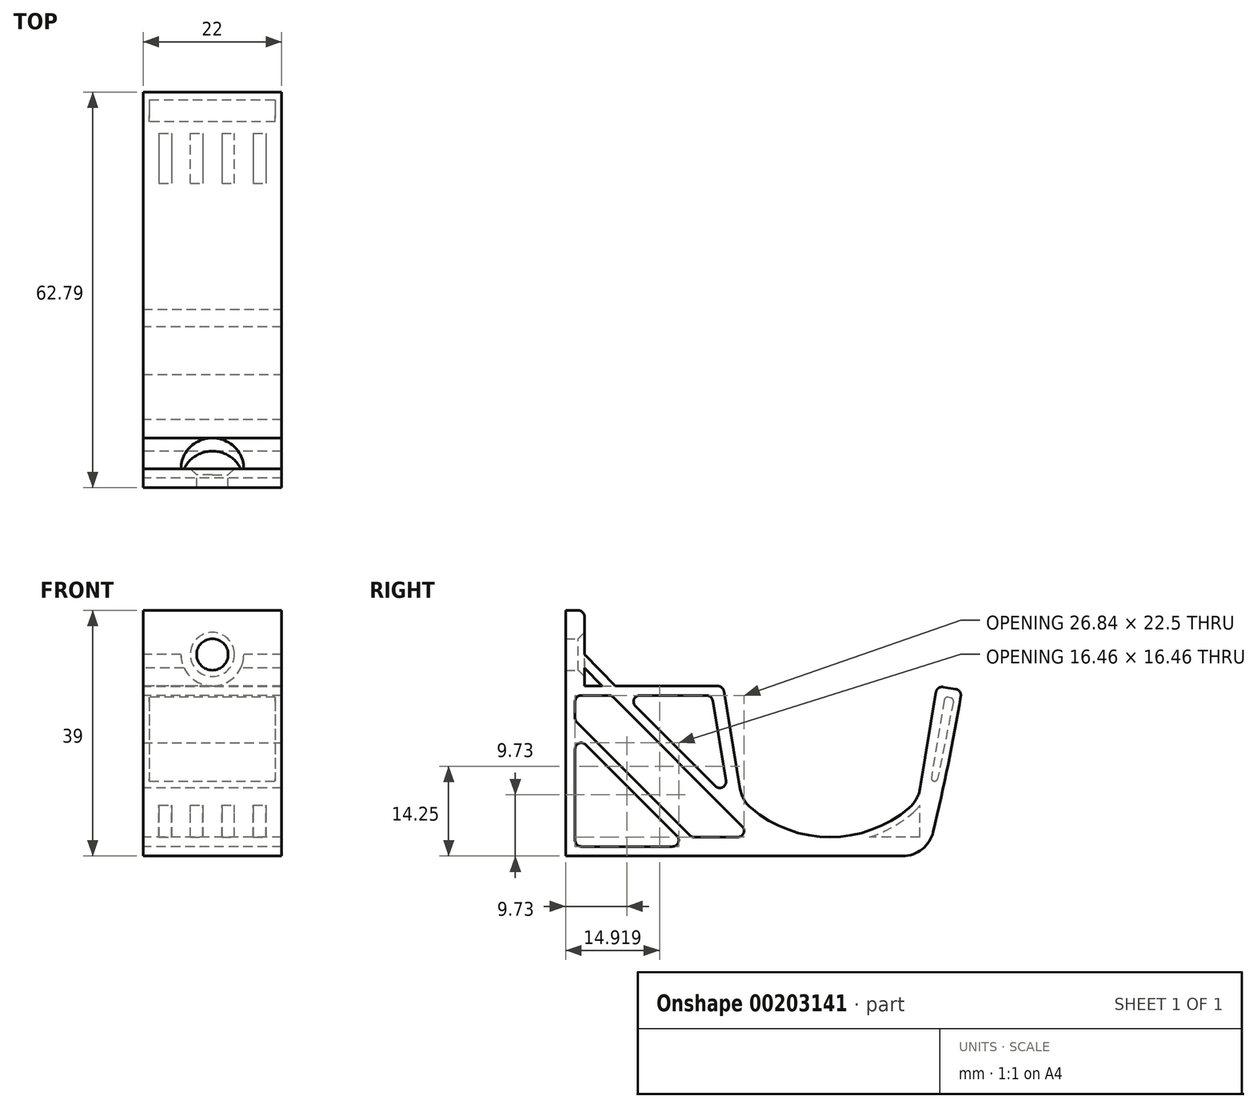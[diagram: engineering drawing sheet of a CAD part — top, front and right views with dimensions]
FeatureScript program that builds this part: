
annotation { "Feature Type Name" : "Feature", "Feature Type Description" : "" }
export const myFeature = defineFeature(function(context is Context, id is Id, definition is map)
    precondition{}
    {
        {
            var Q0;
            Q0=qCreatedBy(makeId("Right.planeOp"),FACE);
            var sketch = newSketch(context, id + "F0", { "sketchPlane" : qUnion([Q0])});
            skLineSegment(sketch, "E0", {"start": v(1.5, 1.5) * mm, "end": v(1.5, 25.5) * mm});
            skLineSegment(sketch, "E1", {"start": v(3, 39) * mm, "end": v(0, 39) * mm});
            skLineSegment(sketch, "E2", {"start": v(0, 39) * mm, "end": v(0, 0) * mm});
            skLineSegment(sketch, "E3", {"start": v(0, 0) * mm, "end": v(57.47, 0) * mm});
            skArc(sketch, "E4", {"start": v(28, 9) * mm, "mid": v(42, 3) * mm, "end": v(56, 9) * mm});
            skLineSegment(sketch, "E5", {"start": v(42, 3) * mm, "end": v(0, 3) * mm, "construction": true});
            skLineSegment(sketch, "E6", {"start": v(42, 22.33) * mm, "end": v(42, 40.34) * mm, "construction": true});
            skLineSegment(sketch, "E7.MirrorCS", {"start": v(28, 9) * mm, "end": v(25, 27) * mm});
            skLineSegment(sketch, "E8.MirrorCS", {"start": v(56, 9) * mm, "end": v(59, 27) * mm});
            skLineSegment(sketch, "E9", {"start": v(59, 27) * mm, "end": v(62.95, 26.34) * mm});
            skArc(sketch, "E10", {"start": v(57.47, 0) * mm, "mid": v(60.47, 13.12) * mm, "end": v(62.95, 26.34) * mm});
            skLineSegment(sketch, "E11", {"start": v(25, 27) * mm, "end": v(3, 27) * mm});
            skLineSegment(sketch, "E12", {"start": v(1.5, 25.5) * mm, "end": v(23.22, 25.5) * mm});
            skLineSegment(sketch, "E13", {"start": v(23.22, 25.5) * mm, "end": v(26, 8.89) * mm});
            skLineSegment(sketch, "E14", {"start": v(19.38, 1.5) * mm, "end": v(1.5, 1.5) * mm});
            skLineSegment(sketch, "E15.trimOffspring", {"start": v(3, 27) * mm, "end": v(3, 39) * mm});
            skLineSegment(sketch, "E16", {"start": v(9.38, 25.5) * mm, "end": v(26, 8.89) * mm});
            skLineSegment(sketch, "E17", {"start": v(7.26, 25.5) * mm, "end": v(29.76, 3) * mm});
            skLineSegment(sketch, "E18", {"start": v(20, 3) * mm, "end": v(1.5, 21.5) * mm});
            skLineSegment(sketch, "E19", {"start": v(1.5, 19.38) * mm, "end": v(19.38, 1.5) * mm});
            skPoint(sketch, "E20", {"position": v(1.5, 13.5) * mm});
            skLineSegment(sketch, "E21", {"start": v(5.78, 27) * mm, "end": v(3, 29.85) * mm});
            skLineSegment(sketch, "E22", {"start": v(7.88, 27) * mm, "end": v(3, 32) * mm});
            skLineSegment(sketch, "E23", {"start": v(26.5, 18) * mm, "end": v(57.5, 18) * mm, "construction": true});
            skLineSegment(sketch, "E24", {"start": v(29.76, 3) * mm, "end": v(20, 3) * mm});
            skLineSegment(sketch, "E25", {"start": v(9.38, 25.5) * mm, "end": v(7.88, 27) * mm, "construction": true});
            skCircle(sketch, "E26", {"center": v(28, 9) * mm, "radius": 3 * mm, "construction": true});
            skSolve(sketch);
        }
        {
            var Q0;
            Q0=makeQuery(id+"F0.imprint","IMPRINT",FACE,{"disambiguationData":[TD([[makeQuery(id+"F0.imprint","IMPRINT",EDGE,{"derivedFrom":sQuery(id+"F0.wireOp",EDGE,"E0")}),1.0]])]});
            var Q1;
            {var subQ0=sQuery(id+"F0.wireOp",EDGE,"E16");Q1=makeQuery(id+"F0.imprint","IMPRINT",FACE,{"disambiguationData":[TD([[makeQuery(id+"F0.imprint","IMPRINT",EDGE,{"derivedFrom":subQ0}),-1.0]])]});}
            var Q2;
            {var subQ0=sQuery(id+"F0.wireOp",EDGE,"E18");Q2=makeQuery(id+"F0.imprint","IMPRINT",FACE,{"disambiguationData":[TD([[makeQuery(id+"F0.imprint","IMPRINT",EDGE,{"derivedFrom":subQ0}),1.0]])]});}
            var Q3;
            {var subQ0=sQuery(id+"F0.wireOp",EDGE,"E21");Q3=makeQuery(id+"F0.imprint","IMPRINT",FACE,{"disambiguationData":[TD([[makeQuery(id+"F0.imprint","IMPRINT",EDGE,{"derivedFrom":subQ0}),-1.0]])]});}
            extrude(context, id + "F1", {"entities" : qUnion([Q0, Q1, Q2, Q3]), "depth" : 22 * mm});
        }
        {
            var Q0;
            Q0=makeQuery(id+"F1.opExtrude","SWEPT_EDGE",EDGE,{"disambiguationData":[OSD([sQuery(id+"F0.wireOp",EDGE,"E3"),sQuery(id+"F0.wireOp",EDGE,"E10")])]});
            var Q1;
            Q1=makeQuery(id+"F1.opExtrude","SWEPT_EDGE",EDGE,{"disambiguationData":[OSD([sQuery(id+"F0.wireOp",EDGE,"E4"),sQuery(id+"F0.wireOp",EDGE,"E8.MirrorCS")])]});
            var Q2;
            Q2=makeQuery(id+"F1.opExtrude","SWEPT_EDGE",EDGE,{"disambiguationData":[OSD([sQuery(id+"F0.wireOp",EDGE,"E4"),sQuery(id+"F0.wireOp",EDGE,"E7.MirrorCS")])]});
            fillet(context, id + "F2", {"entities" : qUnion([Q0, Q1, Q2]), "radius" : 5 * mm, "tangentPropagation" : true, "allowEdgeOverflow" : false});
        }
        {
            var Q0;
            Q0=makeQuery(id+"F1.opExtrude","SWEPT_EDGE",EDGE,{"disambiguationData":[OSD([sQuery(id+"F0.wireOp",EDGE,"E8.MirrorCS"),sQuery(id+"F0.wireOp",EDGE,"E9")])]});
            var Q1;
            Q1=makeQuery(id+"F1.opExtrude","SWEPT_EDGE",EDGE,{"disambiguationData":[OSD([sQuery(id+"F0.wireOp",EDGE,"E9"),sQuery(id+"F0.wireOp",EDGE,"E10")])]});
            var Q2;
            Q2=makeQuery(id+"F1.opExtrude","SWEPT_EDGE",EDGE,{"disambiguationData":[OSD([sQuery(id+"F0.wireOp",EDGE,"E1"),sQuery(id+"F0.wireOp",EDGE,"E15.trimOffspring")])]});
            var Q3;
            Q3=makeQuery(id+"F1.opExtrude","SWEPT_EDGE",EDGE,{"disambiguationData":[OSD([sQuery(id+"F0.wireOp",EDGE,"E7.MirrorCS"),sQuery(id+"F0.wireOp",EDGE,"E11")])]});
            var Q4;
            Q4=makeQuery(id+"F1.opExtrude","SWEPT_EDGE",EDGE,{"disambiguationData":[OSD([sQuery(id+"F0.wireOp",EDGE,"E12"),sQuery(id+"F0.wireOp",EDGE,"E13")])]});
            fillet(context, id + "F3", {"entities" : qUnion([Q0, Q1, Q2, Q3, Q4]), "radius" : 1 * mm, "tangentPropagation" : true, "allowEdgeOverflow" : false});
        }
        {
            var Q0;
            Q0=makeQuery(id+"F1.opExtrude","SWEPT_EDGE",EDGE,{"disambiguationData":[OSD([sQuery(id+"F0.wireOp",EDGE,"E0"),sQuery(id+"F0.wireOp",EDGE,"E14")])]});
            var Q1;
            Q1=makeQuery(id+"F1.opExtrude","SWEPT_EDGE",EDGE,{"disambiguationData":[OSD([sQuery(id+"F0.wireOp",EDGE,"E14"),sQuery(id+"F0.wireOp",EDGE,"E19")])]});
            var Q2;
            Q2=makeQuery(id+"F1.opExtrude","SWEPT_EDGE",EDGE,{"disambiguationData":[OSD([sQuery(id+"F0.wireOp",EDGE,"E0"),sQuery(id+"F0.wireOp",EDGE,"E14")])]});
            var Q3;
            Q3=makeQuery(id+"F1.opExtrude","SWEPT_EDGE",EDGE,{"disambiguationData":[OSD([sQuery(id+"F0.wireOp",EDGE,"E14"),sQuery(id+"F0.wireOp",EDGE,"E19")])]});
            var Q4;
            Q4=makeQuery(id+"F1.opExtrude","SWEPT_EDGE",EDGE,{"disambiguationData":[OSD([sQuery(id+"F0.wireOp",EDGE,"E18"),sQuery(id+"F0.wireOp",EDGE,"E24")])]});
            var Q5;
            Q5=makeQuery(id+"F1.opExtrude","SWEPT_EDGE",EDGE,{"disambiguationData":[OSD([sQuery(id+"F0.wireOp",EDGE,"E0"),sQuery(id+"F0.wireOp",EDGE,"E18")])]});
            var Q6;
            Q6=makeQuery(id+"F1.opExtrude","SWEPT_EDGE",EDGE,{"disambiguationData":[OSD([sQuery(id+"F0.wireOp",EDGE,"E14"),sQuery(id+"F0.wireOp",EDGE,"E19")])]});
            var Q7;
            Q7=makeQuery(id+"F1.opExtrude","SWEPT_EDGE",EDGE,{"disambiguationData":[OSD([sQuery(id+"F0.wireOp",EDGE,"E0"),sQuery(id+"F0.wireOp",EDGE,"E19")])]});
            var Q8;
            Q8=makeQuery(id+"F1.opExtrude","SWEPT_EDGE",EDGE,{"disambiguationData":[OSD([sQuery(id+"F0.wireOp",EDGE,"E0"),sQuery(id+"F0.wireOp",EDGE,"E18")])]});
            var Q9;
            Q9=makeQuery(id+"F1.opExtrude","SWEPT_EDGE",EDGE,{"disambiguationData":[OSD([sQuery(id+"F0.wireOp",EDGE,"E12"),sQuery(id+"F0.wireOp",EDGE,"E17")])]});
            var Q10;
            Q10=makeQuery(id+"F1.opExtrude","SWEPT_EDGE",EDGE,{"disambiguationData":[OSD([sQuery(id+"F0.wireOp",EDGE,"E12"),sQuery(id+"F0.wireOp",EDGE,"E16")])]});
            var Q11;
            Q11=makeQuery(id+"F1.opExtrude","SWEPT_EDGE",EDGE,{"disambiguationData":[OSD([sQuery(id+"F0.wireOp",EDGE,"E13"),sQuery(id+"F0.wireOp",EDGE,"E17"),sQuery(id+"F0.wireOp",EDGE,"E24")])]});
            var Q12;
            Q12=makeQuery(id+"F1.opExtrude","SWEPT_EDGE",EDGE,{"disambiguationData":[OSD([sQuery(id+"F0.wireOp",EDGE,"E0"),sQuery(id+"F0.wireOp",EDGE,"E12")])]});
            var Q13;
            Q13=makeQuery(id+"F1.opExtrude","SWEPT_EDGE",EDGE,{"disambiguationData":[OSD([sQuery(id+"F0.wireOp",EDGE,"E0"),sQuery(id+"F0.wireOp",EDGE,"E14")])]});
            var Q14;
            Q14=makeQuery(id+"F1.opExtrude","SWEPT_EDGE",EDGE,{"disambiguationData":[OSD([sQuery(id+"F0.wireOp",EDGE,"E13"),sQuery(id+"F0.wireOp",EDGE,"E16")])]});
            fillet(context, id + "F4", {"entities" : qUnion([Q0, Q1, Q2, Q3, Q4, Q5, Q6, Q7, Q8, Q9, Q10, Q11, Q12, Q13, Q14]), "radius" : 1 * mm, "tangentPropagation" : true, "allowEdgeOverflow" : false});
        }
        {
            var Q0;
            Q0=qCreatedBy(makeId("Front.planeOp"),FACE);
            cPlane(context, id + "F5", {"entities" : qUnion([Q0]), "cplaneType" : CPlaneType.OFFSET, "offset" : 50 * mm, "oppositeDirection" : true, "width" : 150 * mm, "height" : 150 * mm});
        }
        {
            var Q0;
            Q0=qCreatedBy(id+"F5.planeOp",FACE);
            var sketch = newSketch(context, id + "F6", { "sketchPlane" : qUnion([Q0])});
            skLineSegment(sketch, "E27.0", {"start": v(22, 39) * mm, "end": v(0, 39) * mm, "construction": true});
            skLineSegment(sketch, "E28.0", {"start": v(0, 0) * mm, "end": v(22, 0) * mm, "construction": true});
            skLineSegment(sketch, "E29", {"start": v(0, 0) * mm, "end": v(0, 39) * mm, "construction": true});
            skLineSegment(sketch, "E30", {"start": v(22, 39) * mm, "end": v(22, 0) * mm, "construction": true});
            skLineSegment(sketch, "E31.0", {"start": v(22, 27) * mm, "end": v(0, 27) * mm, "construction": true});
            skCircle(sketch, "E32", {"center": v(11, 32) * mm, "radius": 5 * mm});
            skLineSegment(sketch, "E33", {"start": v(11, 39) * mm, "end": v(11, 27) * mm, "construction": true});
            skLineSegment(sketch, "E34.0", {"start": v(22, 32) * mm, "end": v(0, 32) * mm, "construction": true});
            skLineSegment(sketch, "E35.0", {"start": v(22, 25.5) * mm, "end": v(0, 25.5) * mm, "construction": true});
            skLineSegment(sketch, "E36.0", {"start": v(0, 38) * mm, "end": v(22, 38) * mm, "construction": true});
            skSolve(sketch);
        }
        {
            var Q0;
            Q0 = qSketchRegion(id + "F6", true);
            var Q1;
            {var subQ0=sQuery(id+"F0.wireOp",EDGE,"E15.trimOffspring");Q1=makeQuery(id+"F1.opExtrude","SWEPT_FACE",FACE,{"disambiguationData":[OSD([subQ0]),TDD([makeQuery(id+"F0.imprint","IMPRINT",EDGE,{"disambiguationData":[TD([[makeQuery(id+"F0.imprint","INTERSECT",VERTEX,{"derivedFrom":[sQuery(id+"F0.wireOp",EDGE,"E1"),subQ0]}),1.0]])],"derivedFrom":subQ0})])]});}
            extrude(context, id + "F7", {"entities" : qUnion([Q0]), "operationType" : NewBodyOperationType.REMOVE, "endBound" : BoundingType.UP_TO_SURFACE, "endBoundEntityFace" : qUnion([Q1]), "depth" : 46 * mm});
        }
        {
            var Q0;
            Q0=qCreatedBy(id+"F5.planeOp",FACE);
            var sketch = newSketch(context, id + "F8", { "sketchPlane" : qUnion([Q0])});
            skCircle(sketch, "E37", {"center": v(11, 32) * mm, "radius": 2.5 * mm});
            skSolve(sketch);
        }
        {
            var Q0;
            Q0 = qSketchRegion(id + "F8", true);
            extrude(context, id + "F9", {"entities" : qUnion([Q0]), "operationType" : NewBodyOperationType.REMOVE, "endBound" : BoundingType.THROUGH_ALL, "depth" : 25 * mm});
        }
        {
            var Q0;
            {var subQ0=sQuery(id+"F0.wireOp",EDGE,"E15.trimOffspring");Q0=makeQuery(id+"F9.boolean.opBoolean","INTERSECT",EDGE,{"derivedFrom":[makeQuery(id+"F7.boolean.opBoolean","MERGE",FACE,{"derivedFrom":[makeQuery(id+"F1.opExtrude","SWEPT_FACE",FACE,{"disambiguationData":[OSD([subQ0]),TDD([makeQuery(id+"F0.imprint","IMPRINT",EDGE,{"disambiguationData":[TD([[makeQuery(id+"F0.imprint","INTERSECT",VERTEX,{"derivedFrom":[sQuery(id+"F0.wireOp",EDGE,"E11"),subQ0]}),-1.0]])],"derivedFrom":subQ0})])]}),makeQuery(id+"F1.opExtrude","SWEPT_FACE",FACE,{"disambiguationData":[OSD([subQ0]),TDD([makeQuery(id+"F0.imprint","IMPRINT",EDGE,{"disambiguationData":[TD([[makeQuery(id+"F0.imprint","INTERSECT",VERTEX,{"derivedFrom":[sQuery(id+"F0.wireOp",EDGE,"E1"),subQ0]}),1.0]])],"derivedFrom":subQ0})])]}),makeQuery(id+"F7.opExtrude","CAP_FACE",FACE,{"disambiguationData":[OSD([sQuery(id+"F6.wireOp",EDGE,"E32")])],"isStart":false})]}),makeQuery(id+"F9.opExtrude","SWEPT_FACE",FACE,{"disambiguationData":[OSD([sQuery(id+"F8.wireOp",EDGE,"E37")])]})]});}
            chamfer(context, id + "F10", {"entities" : qUnion([Q0]), "width" : 1 * mm, "tangentPropagation" : true});
        }
        {
            var Q0;
            Q0=qCreatedBy(makeId("Top.planeOp"),FACE);
            cPlane(context, id + "F11", {"entities" : qUnion([Q0]), "cplaneType" : CPlaneType.OFFSET, "offset" : 50 * mm, "width" : 150 * mm, "height" : 150 * mm});
        }
        {
            var Q0;
            Q0=qCreatedBy(id+"F11.planeOp",FACE);
            var sketch = newSketch(context, id + "F12", { "sketchPlane" : qUnion([Q0])});
            skLineSegment(sketch, "E38.0", {"start": v(0, 42) * mm, "end": v(0, 54.6) * mm});
            skLineSegment(sketch, "E39.0", {"start": v(0, 56.27) * mm, "end": v(22, 56.27) * mm});
            skLineSegment(sketch, "E40.0", {"start": v(0, 54.6) * mm, "end": v(0, 56.27) * mm});
            skLineSegment(sketch, "E41.0", {"start": v(22, 42) * mm, "end": v(22, 54.6) * mm});
            skLineSegment(sketch, "E42.0", {"start": v(22, 56.27) * mm, "end": v(22, 54.6) * mm});
            skLineSegment(sketch, "E43", {"start": v(0, 42) * mm, "end": v(22, 42) * mm});
            skPoint(sketch, "E44.orphan", {"position": v(0, 29.4) * mm});
            skPoint(sketch, "E45.orphan", {"position": v(22, 29.4) * mm});
            skLineSegment(sketch, "E46", {"start": v(11, 56.27) * mm, "end": v(11, 42) * mm});
            skLineSegment(sketch, "E47", {"start": v(9.5, 56.27) * mm, "end": v(9.5, 42) * mm});
            skLineSegment(sketch, "E48", {"start": v(7.5, 42) * mm, "end": v(7.5, 56.27) * mm});
            skLineSegment(sketch, "E49", {"start": v(4.5, 56.27) * mm, "end": v(4.5, 42) * mm});
            skLineSegment(sketch, "E50", {"start": v(2.5, 56.27) * mm, "end": v(2.5, 42) * mm});
            skLineSegment(sketch, "E51.MirrorCS", {"start": v(12.5, 56.27) * mm, "end": v(12.5, 42) * mm});
            skLineSegment(sketch, "E52.MirrorCS", {"start": v(14.5, 42) * mm, "end": v(14.5, 56.27) * mm});
            skLineSegment(sketch, "E53.MirrorCS", {"start": v(19.5, 56.27) * mm, "end": v(19.5, 42) * mm});
            skLineSegment(sketch, "E54.MirrorCS", {"start": v(17.5, 56.27) * mm, "end": v(17.5, 42) * mm});
            skSolve(sketch);
        }
        {
            var Q0;
            {var subQ0=sQuery(id+"F12.wireOp",EDGE,"E49");Q0=makeQuery(id+"F12.imprint","IMPRINT",FACE,{"disambiguationData":[TD([[makeQuery(id+"F12.imprint","IMPRINT",EDGE,{"derivedFrom":subQ0}),-1.0]])]});}
            var Q1;
            {var subQ0=sQuery(id+"F12.wireOp",EDGE,"E47");Q1=makeQuery(id+"F12.imprint","IMPRINT",FACE,{"disambiguationData":[TD([[makeQuery(id+"F12.imprint","IMPRINT",EDGE,{"derivedFrom":subQ0}),-1.0]])]});}
            var Q2;
            {var subQ0=sQuery(id+"F12.wireOp",EDGE,"E51.MirrorCS");Q2=makeQuery(id+"F12.imprint","IMPRINT",FACE,{"disambiguationData":[TD([[makeQuery(id+"F12.imprint","IMPRINT",EDGE,{"derivedFrom":subQ0}),1.0]])]});}
            var Q3;
            {var subQ0=sQuery(id+"F12.wireOp",EDGE,"E53.MirrorCS");Q3=makeQuery(id+"F12.imprint","IMPRINT",FACE,{"disambiguationData":[TD([[makeQuery(id+"F12.imprint","IMPRINT",EDGE,{"derivedFrom":subQ0}),-1.0]])]});}
            extrude(context, id + "F13", {"entities" : qUnion([Q0, Q1, Q2, Q3]), "operationType" : NewBodyOperationType.REMOVE, "oppositeDirection" : true, "depth" : 47 * mm});
        }
        {
            var Q0;
            Q0=qCreatedBy(makeId("Right.planeOp"),FACE);
            cPlane(context, id + "F14", {"entities" : qUnion([Q0]), "cplaneType" : CPlaneType.OFFSET, "offset" : 11 * mm, "width" : 150 * mm, "height" : 150 * mm});
        }
        {
            var Q0;
            Q0=qCreatedBy(id+"F14.planeOp",FACE);
            var sketch = newSketch(context, id + "F15", { "sketchPlane" : qUnion([Q0])});
            skLineSegment(sketch, "E55", {"start": v(60.23, 25.27) * mm, "end": v(58.01, 11.97) * mm});
            skLineSegment(sketch, "E56", {"start": v(58.01, 11.97) * mm, "end": v(59, 11.8) * mm});
            skLineSegment(sketch, "E57", {"start": v(61.7, 25.03) * mm, "end": v(60.23, 25.27) * mm});
            skLineSegment(sketch, "E58", {"start": v(62.78, 25.35) * mm, "end": v(58.4, 3.84) * mm, "construction": true});
            skLineSegment(sketch, "E59", {"start": v(61.7, 25.03) * mm, "end": v(59, 11.8) * mm});
            skSolve(sketch);
        }
        {
            var Q0;
            Q0 = qSketchRegion(id + "F15", true);
            extrude(context, id + "F16", {"entities" : qUnion([Q0]), "operationType" : NewBodyOperationType.REMOVE, "endBound" : BoundingType.SYMMETRIC, "oppositeDirection" : true, "depth" : 20 * mm});
        }
        {
            var Q0;
            Q0=makeQuery(id+"F16.boolean.opBoolean","COPY",EDGE,{"derivedFrom":makeQuery(id+"F16.opExtrude","SWEPT_EDGE",EDGE,{"disambiguationData":[OSD([sQuery(id+"F15.wireOp",EDGE,"E56"),sQuery(id+"F15.wireOp",EDGE,"E59")])]})});
            var Q1;
            Q1=makeQuery(id+"F16.boolean.opBoolean","COPY",EDGE,{"derivedFrom":makeQuery(id+"F16.opExtrude","SWEPT_EDGE",EDGE,{"disambiguationData":[OSD([sQuery(id+"F15.wireOp",EDGE,"E55"),sQuery(id+"F15.wireOp",EDGE,"E57")])]})});
            var Q2;
            Q2=makeQuery(id+"F16.boolean.opBoolean","COPY",EDGE,{"derivedFrom":makeQuery(id+"F16.opExtrude","SWEPT_EDGE",EDGE,{"disambiguationData":[OSD([sQuery(id+"F15.wireOp",EDGE,"E57"),sQuery(id+"F15.wireOp",EDGE,"E59")])]})});
            var Q3;
            Q3=makeQuery(id+"F16.boolean.opBoolean","COPY",EDGE,{"derivedFrom":makeQuery(id+"F16.opExtrude","SWEPT_EDGE",EDGE,{"disambiguationData":[OSD([sQuery(id+"F15.wireOp",EDGE,"E55"),sQuery(id+"F15.wireOp",EDGE,"E56")])]})});
            fillet(context, id + "F17", {"entities" : qUnion([Q0, Q1, Q2, Q3]), "radius" : .5 * mm, "tangentPropagation" : true, "allowEdgeOverflow" : false});
        }
        {
            var Q0;
            Q0=makeQuery(id+"F1.opExtrude","CAP_FACE",FACE,{"disambiguationData":[OSD([sQuery(id+"F0.wireOp",EDGE,"E0"),sQuery(id+"F0.wireOp",EDGE,"E1"),sQuery(id+"F0.wireOp",EDGE,"E2"),sQuery(id+"F0.wireOp",EDGE,"E3"),sQuery(id+"F0.wireOp",EDGE,"E4"),sQuery(id+"F0.wireOp",EDGE,"E7.MirrorCS"),sQuery(id+"F0.wireOp",EDGE,"E8.MirrorCS"),sQuery(id+"F0.wireOp",EDGE,"E9"),sQuery(id+"F0.wireOp",EDGE,"E10"),sQuery(id+"F0.wireOp",EDGE,"E11"),sQuery(id+"F0.wireOp",EDGE,"E12"),sQuery(id+"F0.wireOp",EDGE,"E13"),sQuery(id+"F0.wireOp",EDGE,"E14"),sQuery(id+"F0.wireOp",EDGE,"E15.trimOffspring"),sQuery(id+"F0.wireOp",EDGE,"E16"),sQuery(id+"F0.wireOp",EDGE,"E17"),sQuery(id+"F0.wireOp",EDGE,"E18"),sQuery(id+"F0.wireOp",EDGE,"E19"),sQuery(id+"F0.wireOp",EDGE,"E21"),sQuery(id+"F0.wireOp",EDGE,"E22"),sQuery(id+"F0.wireOp",EDGE,"E24")])],"isStart":false});
            var sketch = newSketch(context, id + "F18", { "sketchPlane" : qUnion([Q0])});
            skArc(sketch, "E60.0", {"start": v(29.4, 7.67) * mm, "mid": v(42, 3) * mm, "end": v(54.6, 7.67) * mm});
            skPoint(sketch, "E61.0", {"position": v(55.7, 9) * mm});
            skArc(sketch, "E62.0", {"start": v(56.27, 10.64) * mm, "mid": v(55.7, 9) * mm, "end": v(54.6, 7.67) * mm});
            skArc(sketch, "E63.0", {"start": v(57.26, 10.48) * mm, "mid": v(56.57, 8.52) * mm, "end": v(55.25, 6.91) * mm});
            skArc(sketch, "E63.1", {"start": v(28.75, 6.91) * mm, "mid": v(42, 2) * mm, "end": v(55.25, 6.91) * mm});
            skLineSegment(sketch, "E64", {"start": v(28.75, 6.91) * mm, "end": v(29.4, 7.67) * mm});
            skLineSegment(sketch, "E65", {"start": v(57.26, 10.48) * mm, "end": v(56.27, 10.64) * mm});
            skSolve(sketch);
        }
        {
            var Q0;
            Q0 = qSketchRegion(id + "F18", true);
            var Q1;
            Q1=makeQuery(id+"F1.opExtrude","CAP_FACE",FACE,{"disambiguationData":[OSD([sQuery(id+"F0.wireOp",EDGE,"E0"),sQuery(id+"F0.wireOp",EDGE,"E1"),sQuery(id+"F0.wireOp",EDGE,"E2"),sQuery(id+"F0.wireOp",EDGE,"E3"),sQuery(id+"F0.wireOp",EDGE,"E4"),sQuery(id+"F0.wireOp",EDGE,"E7.MirrorCS"),sQuery(id+"F0.wireOp",EDGE,"E8.MirrorCS"),sQuery(id+"F0.wireOp",EDGE,"E9"),sQuery(id+"F0.wireOp",EDGE,"E10"),sQuery(id+"F0.wireOp",EDGE,"E11"),sQuery(id+"F0.wireOp",EDGE,"E12"),sQuery(id+"F0.wireOp",EDGE,"E13"),sQuery(id+"F0.wireOp",EDGE,"E14"),sQuery(id+"F0.wireOp",EDGE,"E15.trimOffspring"),sQuery(id+"F0.wireOp",EDGE,"E16"),sQuery(id+"F0.wireOp",EDGE,"E17"),sQuery(id+"F0.wireOp",EDGE,"E18"),sQuery(id+"F0.wireOp",EDGE,"E19"),sQuery(id+"F0.wireOp",EDGE,"E21"),sQuery(id+"F0.wireOp",EDGE,"E22"),sQuery(id+"F0.wireOp",EDGE,"E24")])],"isStart":true});
            extrude(context, id + "F19", {"entities" : qUnion([Q0]), "operationType" : NewBodyOperationType.ADD, "endBound" : BoundingType.UP_TO_SURFACE, "oppositeDirection" : true, "endBoundEntityFace" : qUnion([Q1]), "depth" : 25 * mm});
        }
    });
